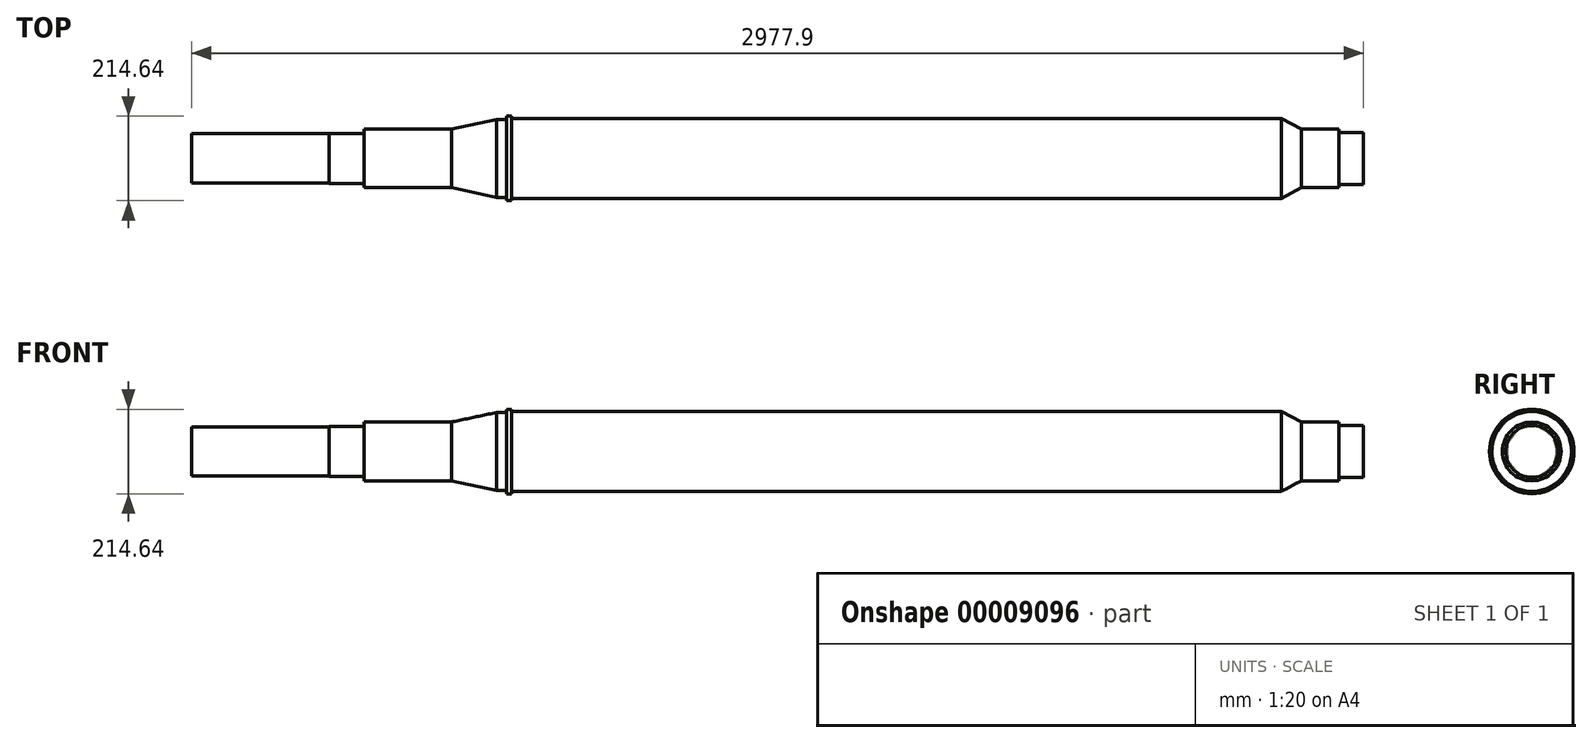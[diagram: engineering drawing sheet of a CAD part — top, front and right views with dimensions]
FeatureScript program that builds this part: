
annotation { "Feature Type Name" : "Feature", "Feature Type Description" : "" }
export const myFeature = defineFeature(function(context is Context, id is Id, definition is map)
    precondition{}
    {
        {
            var Q0;
            Q0=qCreatedBy(makeId("Right.planeOp"),FACE);
            var sketch = newSketch(context, id + "F0", { "sketchPlane" : qUnion([Q0])});
            skCircle(sketch, "E0", {"center": v(0, 0) * mm, "radius": 101.6 * mm});
            skSolve(sketch);
        }
        {
            var Q0;
            Q0 = qSketchRegion(id + "F0", true);
            extrude(context, id + "F1", {"entities" : qUnion([Q0]), "endBound" : BoundingType.SYMMETRIC, "depth" : 1955.8 * mm});
        }
        {
            var Q0;
            Q0=makeQuery(id+"F1.opExtrude","CAP_FACE",FACE,{"disambiguationData":[OSD([sQuery(id+"F0.wireOp",EDGE,"E0")])],"isStart":false});
            cPlane(context, id + "F2", {"entities" : qUnion([Q0]), "cplaneType" : CPlaneType.OFFSET, "offset" : 0 * mm, "width" : 152.4 * mm, "height" : 152.4 * mm});
        }
        {
            var Q0;
            Q0=makeQuery(id+"F1.opExtrude","CAP_FACE",FACE,{"disambiguationData":[OSD([sQuery(id+"F0.wireOp",EDGE,"E0")])],"isStart":false});
            cPlane(context, id + "F3", {"entities" : qUnion([Q0]), "cplaneType" : CPlaneType.OFFSET, "offset" : 50.8 * mm, "width" : 152.4 * mm, "height" : 152.4 * mm});
        }
        {
            var Q0;
            Q0=qCreatedBy(id+"F2.planeOp",FACE);
            var sketch = newSketch(context, id + "F4", { "sketchPlane" : qUnion([Q0])});
            skCircle(sketch, "E1.0", {"center": v(0, 0) * mm, "radius": 101.6 * mm});
            skSolve(sketch);
        }
        {
            var Q0;
            Q0=qCreatedBy(id+"F3.planeOp",FACE);
            var sketch = newSketch(context, id + "F5", { "sketchPlane" : qUnion([Q0])});
            skCircle(sketch, "E2", {"center": v(0, 0) * mm, "radius": 74.61 * mm});
            skSolve(sketch);
        }
        {
            var Q1;
            Q1=makeQuery(id+"F4.imprint","IMPRINT",FACE,{"disambiguationData":[TD([[makeQuery(id+"F4.imprint","IMPRINT",EDGE,{"derivedFrom":sQuery(id+"F4.wireOp",EDGE,"E1.0")}),1.0]])]});
            var Q2;
            Q2=makeQuery(id+"F5.imprint","IMPRINT",FACE,{"disambiguationData":[TD([[makeQuery(id+"F5.imprint","IMPRINT",EDGE,{"derivedFrom":sQuery(id+"F5.wireOp",EDGE,"E2")}),1.0]])]});
            loft(context, id + "F6", {"operationType" : NewBodyOperationType.ADD, "sheetProfilesArray" : [{ "sheetProfileEntities" : qUnion([Q1]) }, { "sheetProfileEntities" : qUnion([Q2]) }]});
        }
        {
            var Q0;
            Q0=makeQuery(id+"F6.opLoft","CAP_FACE",FACE,{"disambiguationData":[OSD([makeQuery(id+"F5.imprint","IMPRINT",FACE,{"disambiguationData":[TD([[makeQuery(id+"F5.imprint","IMPRINT",EDGE,{"derivedFrom":sQuery(id+"F5.wireOp",EDGE,"E2")}),1.0]])]})])],"isStart":true});
            extrude(context, id + "F7", {"entities" : qUnion([Q0]), "operationType" : NewBodyOperationType.ADD, "depth" : 95.25 * mm});
        }
        {
            var Q0;
            Q0=makeQuery(id+"F7.opExtrude","CAP_FACE",FACE,{"disambiguationData":[OSD([makeQuery(id+"F5.imprint","IMPRINT",FACE,{"disambiguationData":[TD([[makeQuery(id+"F5.imprint","IMPRINT",EDGE,{"derivedFrom":sQuery(id+"F5.wireOp",EDGE,"E2")}),1.0]])]})])],"isStart":false});
            var sketch = newSketch(context, id + "F8", { "sketchPlane" : qUnion([Q0])});
            skCircle(sketch, "E3", {"center": v(0, 0) * mm, "radius": 66.04 * mm});
            skSolve(sketch);
        }
        {
            var Q0;
            Q0 = qSketchRegion(id + "F8", true);
            extrude(context, id + "F9", {"entities" : qUnion([Q0]), "operationType" : NewBodyOperationType.ADD, "depth" : 63.25 * mm});
        }
        {
            var Q0;
            Q0=makeQuery(id+"F1.opExtrude","CAP_FACE",FACE,{"disambiguationData":[OSD([sQuery(id+"F0.wireOp",EDGE,"E0")])],"isStart":true});
            var sketch = newSketch(context, id + "F10", { "sketchPlane" : qUnion([Q0])});
            skCircle(sketch, "E4", {"center": v(0, 0) * mm, "radius": 107.32 * mm});
            skSolve(sketch);
        }
        {
            var Q0;
            Q0 = qSketchRegion(id + "F10", true);
            extrude(context, id + "F11", {"entities" : qUnion([Q0]), "operationType" : NewBodyOperationType.ADD, "depth" : 12.7 * mm});
        }
        {
            var Q0;
            Q0=makeQuery(id+"F11.opExtrude","CAP_FACE",FACE,{"disambiguationData":[OSD([sQuery(id+"F10.wireOp",EDGE,"E4")])],"isStart":false});
            var sketch = newSketch(context, id + "F12", { "sketchPlane" : qUnion([Q0])});
            skCircle(sketch, "E5", {"center": v(0, 0) * mm, "radius": 99.19 * mm});
            skSolve(sketch);
        }
        {
            var Q0;
            Q0 = qSketchRegion(id + "F12", true);
            extrude(context, id + "F13", {"entities" : qUnion([Q0]), "operationType" : NewBodyOperationType.ADD, "depth" : 25.4 * mm});
        }
        {
            var Q0;
            Q0=makeQuery(id+"F13.opExtrude","CAP_FACE",FACE,{"disambiguationData":[OSD([sQuery(id+"F12.wireOp",EDGE,"E5")])],"isStart":false});
            cPlane(context, id + "F14", {"entities" : qUnion([Q0]), "cplaneType" : CPlaneType.OFFSET, "offset" : 114.3 * mm, "width" : 152.4 * mm, "height" : 152.4 * mm});
        }
        {
            var Q0;
            Q0=qCreatedBy(id+"F14.planeOp",FACE);
            var sketch = newSketch(context, id + "F15", { "sketchPlane" : qUnion([Q0])});
            skCircle(sketch, "E6", {"center": v(0, 0) * mm, "radius": 74.61 * mm});
            skSolve(sketch);
        }
        {
            var Q1;
            Q1=makeQuery(id+"F13.opExtrude","CAP_FACE",FACE,{"disambiguationData":[OSD([sQuery(id+"F12.wireOp",EDGE,"E5")])],"isStart":false});
            var Q2;
            Q2=makeQuery(id+"F15.imprint","IMPRINT",FACE,{"disambiguationData":[TD([[makeQuery(id+"F15.imprint","IMPRINT",EDGE,{"derivedFrom":sQuery(id+"F15.wireOp",EDGE,"E6")}),1.0]])]});
            loft(context, id + "F16", {"operationType" : NewBodyOperationType.ADD, "sheetProfilesArray" : [{ "sheetProfileEntities" : qUnion([Q1]) }, { "sheetProfileEntities" : qUnion([Q2]) }]});
        }
        {
            var Q0;
            Q0=makeQuery(id+"F16.opLoft","CAP_FACE",FACE,{"disambiguationData":[OSD([makeQuery(id+"F15.imprint","IMPRINT",FACE,{"disambiguationData":[TD([[makeQuery(id+"F15.imprint","IMPRINT",EDGE,{"derivedFrom":sQuery(id+"F15.wireOp",EDGE,"E6")}),1.0]])]})])],"isStart":true});
            extrude(context, id + "F17", {"entities" : qUnion([Q0]), "operationType" : NewBodyOperationType.ADD, "depth" : 222.25 * mm});
        }
        {
            var Q0;
            Q0=makeQuery(id+"F17.opExtrude","CAP_FACE",FACE,{"disambiguationData":[OSD([makeQuery(id+"F15.imprint","IMPRINT",FACE,{"disambiguationData":[TD([[makeQuery(id+"F15.imprint","IMPRINT",EDGE,{"derivedFrom":sQuery(id+"F15.wireOp",EDGE,"E6")}),1.0]])]})])],"isStart":false});
            var sketch = newSketch(context, id + "F18", { "sketchPlane" : qUnion([Q0])});
            skCircle(sketch, "E7", {"center": v(0, 0) * mm, "radius": 63.5 * mm});
            skSolve(sketch);
        }
        {
            var Q0;
            Q0 = qSketchRegion(id + "F18", true);
            extrude(context, id + "F19", {"entities" : qUnion([Q0]), "operationType" : NewBodyOperationType.ADD, "depth" : 88.9 * mm});
        }
        {
            var Q0;
            Q0=makeQuery(id+"F19.opExtrude","CAP_FACE",FACE,{"disambiguationData":[OSD([sQuery(id+"F18.wireOp",EDGE,"E7")])],"isStart":false});
            var sketch = newSketch(context, id + "F20", { "sketchPlane" : qUnion([Q0])});
            skCircle(sketch, "E8", {"center": v(0, 0) * mm, "radius": 62.61 * mm});
            skSolve(sketch);
        }
        {
            var Q0;
            Q0 = qSketchRegion(id + "F20", true);
            extrude(context, id + "F21", {"entities" : qUnion([Q0]), "operationType" : NewBodyOperationType.ADD, "depth" : 349.25 * mm});
        }
    });
